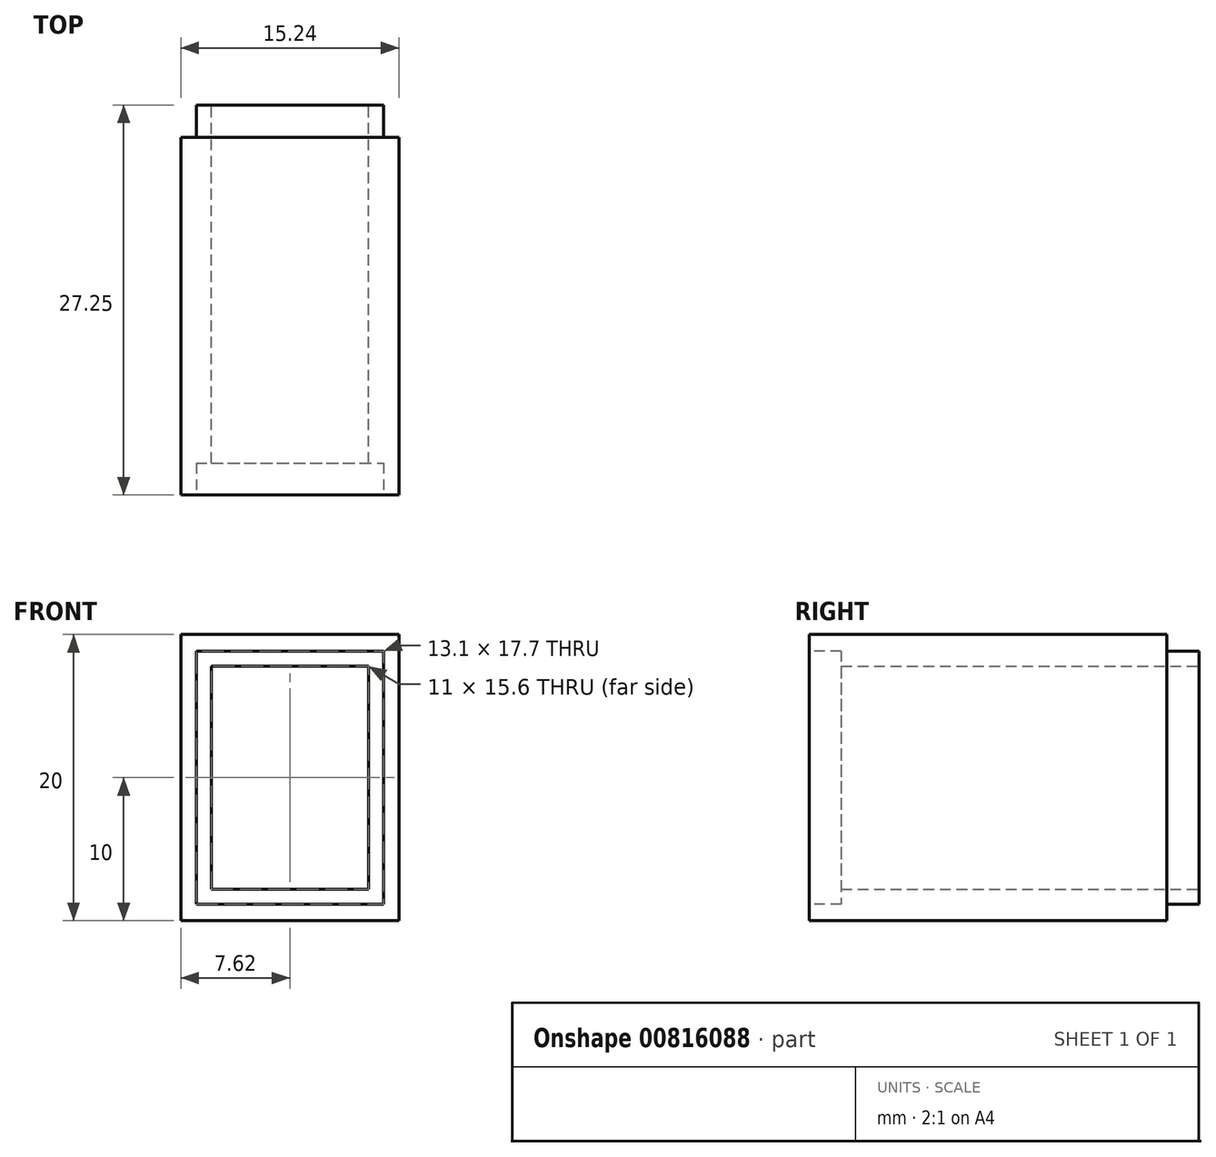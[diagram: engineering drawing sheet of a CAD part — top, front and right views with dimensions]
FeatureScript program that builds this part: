
annotation { "Feature Type Name" : "Feature", "Feature Type Description" : "" }
export const myFeature = defineFeature(function(context is Context, id is Id, definition is map)
    precondition{}
    {
        {
            var Q0;
            Q0=qCreatedBy(makeId("Front.planeOp"),FACE);
            var sketch = newSketch(context, id + "F0", { "sketchPlane" : qUnion([Q0])});
            skLineSegment(sketch, "E0.bottom", {"start": v(-7.62, 10) * mm, "end": v(7.62, 10) * mm});
            skLineSegment(sketch, "E0.top", {"start": v(-7.62, -10) * mm, "end": v(7.62, -10) * mm});
            skLineSegment(sketch, "E0.left", {"start": v(-7.62, 10) * mm, "end": v(-7.62, -10) * mm});
            skLineSegment(sketch, "E0.right", {"start": v(7.62, 10) * mm, "end": v(7.62, -10) * mm});
            skLineSegment(sketch, "E1.bottom", {"start": v(-5.5, 7.8) * mm, "end": v(5.5, 7.8) * mm});
            skLineSegment(sketch, "E1.top", {"start": v(-5.5, -7.8) * mm, "end": v(5.5, -7.8) * mm});
            skLineSegment(sketch, "E1.left", {"start": v(-5.5, 7.8) * mm, "end": v(-5.5, -7.8) * mm});
            skLineSegment(sketch, "E1.right", {"start": v(5.5, 7.8) * mm, "end": v(5.5, -7.8) * mm});
            skSolve(sketch);
        }
        {
            var Q0;
            Q0 = qSketchRegion(id + "F0", true);
            extrude(context, id + "F1", {"entities" : qUnion([Q0]), "depth" : 25 * mm, "offsetDistance" : 25 * mm});
        }
        {
            var Q0;
            Q0=makeQuery(id+"F1.opExtrude","CAP_FACE",FACE,{"disambiguationData":[OSD([sQuery(id+"F0.wireOp",EDGE,"E0.bottom"),sQuery(id+"F0.wireOp",EDGE,"E0.top"),sQuery(id+"F0.wireOp",EDGE,"E0.left"),sQuery(id+"F0.wireOp",EDGE,"E0.right"),sQuery(id+"F0.wireOp",EDGE,"E1.bottom"),sQuery(id+"F0.wireOp",EDGE,"E1.top"),sQuery(id+"F0.wireOp",EDGE,"E1.left"),sQuery(id+"F0.wireOp",EDGE,"E1.right")])],"isStart":true});
            var sketch = newSketch(context, id + "F2", { "sketchPlane" : qUnion([Q0])});
            skLineSegment(sketch, "E2.bottom", {"start": v(-6.55, 8.85) * mm, "end": v(6.55, 8.85) * mm});
            skLineSegment(sketch, "E2.top", {"start": v(-6.55, -8.85) * mm, "end": v(6.55, -8.85) * mm});
            skLineSegment(sketch, "E2.left", {"start": v(-6.55, 8.85) * mm, "end": v(-6.55, -8.85) * mm});
            skLineSegment(sketch, "E2.right", {"start": v(6.55, 8.85) * mm, "end": v(6.55, -8.85) * mm});
            skLineSegment(sketch, "E3.bottom", {"start": v(-5.5, 7.8) * mm, "end": v(5.5, 7.8) * mm});
            skLineSegment(sketch, "E3.top", {"start": v(-5.5, -7.8) * mm, "end": v(5.5, -7.8) * mm});
            skLineSegment(sketch, "E3.left", {"start": v(-5.5, 7.8) * mm, "end": v(-5.5, -7.8) * mm});
            skLineSegment(sketch, "E3.right", {"start": v(5.5, 7.8) * mm, "end": v(5.5, -7.8) * mm});
            skSolve(sketch);
        }
        {
            var Q0;
            Q0=makeQuery(id+"F2.imprint","IMPRINT",FACE,{"disambiguationData":[TD([[makeQuery(id+"F2.imprint","IMPRINT",EDGE,{"derivedFrom":sQuery(id+"F2.wireOp",EDGE,"E2.bottom")}),-1.0]])]});
            extrude(context, id + "F3", {"entities" : qUnion([Q0]), "operationType" : NewBodyOperationType.ADD, "depth" : 2.25 * mm, "offsetDistance" : 25 * mm});
        }
        {
            var Q0;
            Q0=makeQuery(id+"F1.opExtrude","CAP_FACE",FACE,{"disambiguationData":[OSD([sQuery(id+"F0.wireOp",EDGE,"E0.bottom"),sQuery(id+"F0.wireOp",EDGE,"E0.top"),sQuery(id+"F0.wireOp",EDGE,"E0.left"),sQuery(id+"F0.wireOp",EDGE,"E0.right"),sQuery(id+"F0.wireOp",EDGE,"E1.bottom"),sQuery(id+"F0.wireOp",EDGE,"E1.top"),sQuery(id+"F0.wireOp",EDGE,"E1.left"),sQuery(id+"F0.wireOp",EDGE,"E1.right")])],"isStart":false});
            var sketch = newSketch(context, id + "F4", { "sketchPlane" : qUnion([Q0])});
            skLineSegment(sketch, "E4.bottom", {"start": v(-6.55, 8.85) * mm, "end": v(6.55, 8.85) * mm});
            skLineSegment(sketch, "E4.top", {"start": v(-6.55, -8.85) * mm, "end": v(6.55, -8.85) * mm});
            skLineSegment(sketch, "E4.left", {"start": v(-6.55, 8.85) * mm, "end": v(-6.55, -8.85) * mm});
            skLineSegment(sketch, "E4.right", {"start": v(6.55, 8.85) * mm, "end": v(6.55, -8.85) * mm});
            skLineSegment(sketch, "E5.bottom", {"start": v(-5.5, 7.8) * mm, "end": v(5.5, 7.8) * mm});
            skLineSegment(sketch, "E5.top", {"start": v(-5.5, -7.8) * mm, "end": v(5.5, -7.8) * mm});
            skLineSegment(sketch, "E5.left", {"start": v(-5.5, 7.8) * mm, "end": v(-5.5, -7.8) * mm});
            skLineSegment(sketch, "E5.right", {"start": v(5.5, 7.8) * mm, "end": v(5.5, -7.8) * mm});
            skSolve(sketch);
        }
        {
            var Q0;
            Q0 = qSketchRegion(id + "F4", true);
            extrude(context, id + "F5", {"entities" : qUnion([Q0]), "operationType" : NewBodyOperationType.REMOVE, "oppositeDirection" : true, "depth" : 2.25 * mm, "offsetDistance" : 25 * mm});
        }
    });
